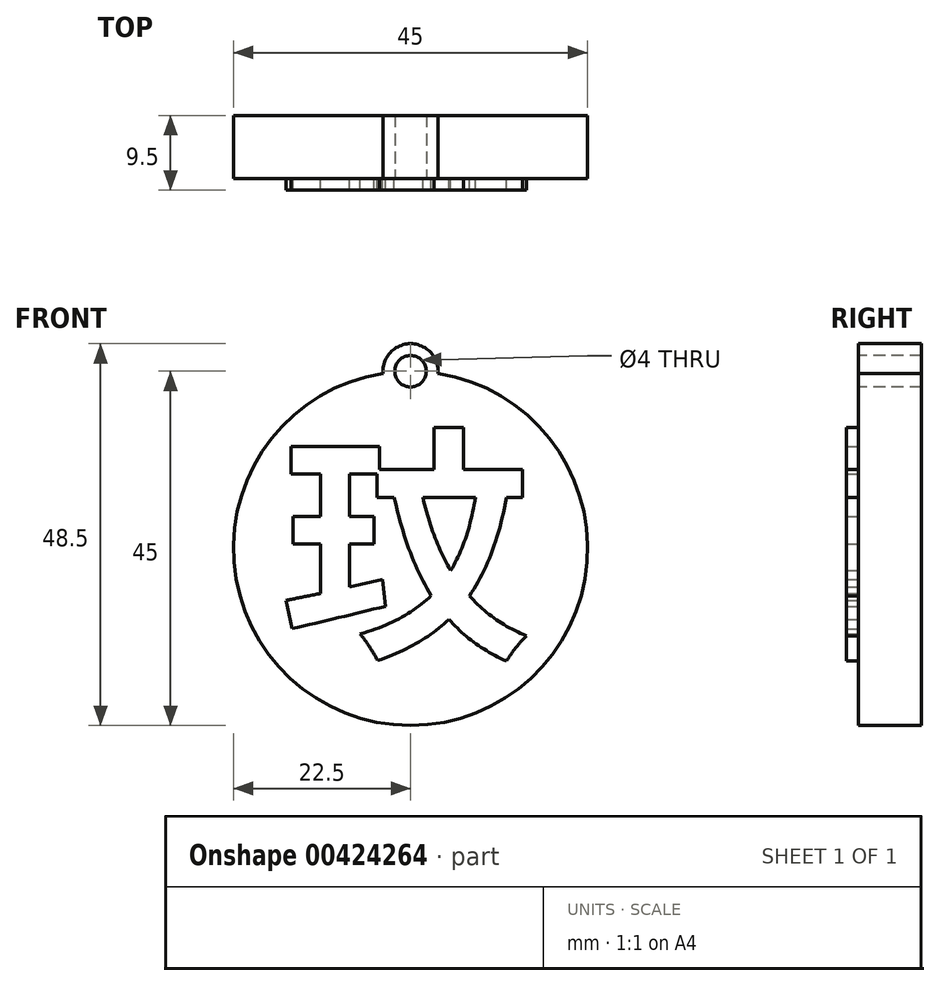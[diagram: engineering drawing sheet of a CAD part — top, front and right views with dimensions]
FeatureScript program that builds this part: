
annotation { "Feature Type Name" : "Feature", "Feature Type Description" : "" }
export const myFeature = defineFeature(function(context is Context, id is Id, definition is map)
    precondition{}
    {
        {
            var Q0;
            Q0=qCreatedBy(makeId("Front.planeOp"),FACE);
            var sketch = newSketch(context, id + "F0", { "sketchPlane" : qUnion([Q0])});
            skArc(sketch, "E0", {"start": v(-3.49, 22.23) * mm, "mid": v(0, -22.5) * mm, "end": v(3.49, 22.23) * mm});
            skArc(sketch, "E1", {"start": v(3.49, 22.23) * mm, "mid": v(0, 26) * mm, "end": v(-3.49, 22.23) * mm});
            skCircle(sketch, "E2", {"center": v(0, 22.5) * mm, "radius": 2 * mm});
            skSolve(sketch);
        }
        {
            var Q0;
            Q0=qCreatedBy(makeId("Front.planeOp"),FACE);
            var sketch = newSketch(context, id + "F1", { "sketchPlane" : qUnion([Q0])});
            skText(sketch, "E3", { "text": "玟", "fontName": "NotoSansCJKjp-Bold.otf"});
            const initialGuessF1  = {"E3": [-0.01649, -0.01151, 1, 0, 0.023]};
            skSetInitialGuess(sketch, initialGuessF1);
            skSolve(sketch);
        }
        {
            var Q0;
            Q0 = qSketchRegion(id + "F1", true);
            extrude(context, id + "F2", {"entities" : qUnion([Q0]), "endBound" : BoundingType.SYMMETRIC, "depth" : 3 * mm});
        }
        {
            var Q0;
            Q0 = qSketchRegion(id + "F0", true);
            extrude(context, id + "F3", {"entities" : qUnion([Q0]), "operationType" : NewBodyOperationType.ADD, "oppositeDirection" : true, "depth" : 8 * mm});
        }
    });
